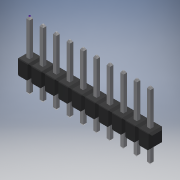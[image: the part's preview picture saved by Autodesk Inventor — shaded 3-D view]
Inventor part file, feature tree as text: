
AUTODESK INVENTOR PART (.ipt)
format: ipt  version: 2018 (Build 220112000, 112)  size: 456,704 bytes
history: native  units: mm
features: other x20, shell x10, sketch x1
ambient origin geometry x8: Origin, YZ Plane, XZ Plane, XY Plane, X Axis, Y Axis, Z Axis, Center Point
bodies: Solid1 (feature_tree), Solid2 (feature_tree), Solid3 (feature_tree), Solid4 (feature_tree), Solid5 (feature_tree), Solid6 (feature_tree), Solid7 (feature_tree), Solid8 (feature_tree), Solid9 (feature_tree), Solid10 (feature_tree)
feature tree (31):
  sketch  "Sketch1"
  other  "brep_1"
  other  "brep_2"
  other  "brep_3"
  other  "brep_4"
  other  "brep_5"
  other  "brep_6"
  other  "brep_7"
  other  "brep_8"
  other  "brep_9"
  other  "brep_10"
  shell  "shell_1"  [1 undecoded]
  shell  "shell_2"  [1 undecoded]
  shell  "shell_3"  [1 undecoded]
  shell  "shell_4"  [1 undecoded]
  shell  "shell_5"  [1 undecoded]
  shell  "shell_6"  [1 undecoded]
  shell  "shell_7"  [1 undecoded]
  shell  "shell_8"  [1 undecoded]
  shell  "shell_9"  [1 undecoded]
  shell  "shell_10"  [1 undecoded]
  other  "Srf1"
  other  "Srf2"
  other  "Srf3"
  other  "Srf4"
  other  "Srf5"
  other  "Srf6"
  other  "Srf7"
  other  "Srf8"
  other  "Srf9"
  other  "Srf10"
note: 10 required parameter values undecoded (feature->parameter linkage not recoverable at this tier; creation-order binding heuristic only, values carry confidence <= 0.55)
